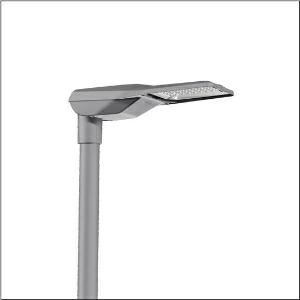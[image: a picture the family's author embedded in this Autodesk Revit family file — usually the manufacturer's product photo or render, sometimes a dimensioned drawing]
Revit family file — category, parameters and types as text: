
# Revit family: streetlight_sl_21_iq_mini___st1_0a_5xe2d41g08hb_63a2
name_source: partatom
category: Lighting Fixtures
units: mm (PartAtom-declared; Revit-internal decimal feet)

## family parameters
Cut with Voids When Loaded = No
Host = Face
Light Source = No
Part Type = Normal
Room Calculation Point = No
Round Connector Dimension = Use Diameter
Shared = No

## types (1)
- --- (1 x LED, 9860 lm, 70.9 W, 4000K)
    Apparent Load = 71 VA
    CIE Flux Codes = 37 72 97 100 100
    Color Rendering = 70
    Color Temperature = 4000K
    Default Elevation = 1800 mm
    Description = Streetlight SL 21 iQ mini, mast luminaire, primary light control with lens, of PMMA, primary optical cover: cover, of toughened safety glass, transparent, light distribution: ST1.0a, light emission: direct distribution, primary light characteristic: asymmetric, installation type: post-top, side-entry, LED, High Power LED, rated luminous flux: 9.860lm, luminous efficacy: 139lm/W, light colour: 740, colour temperature: 4000K, control: Street-Remote, Auto-Match, Temp-Guard, Lumen-Switch, Night-Set, Smart-Wire, Light-Fading, Desk-Remote (wireless, voltage-free reading and setting of iQ features in the workshop via application-optimized NFC function/RFID function), optimised constant luminous flux control (CLO 2.0), presetting dimming linear, mains connection: 220..240V, AC, 50/60Hz, start of lifetime: 71W, end of service life: 75W, reduction: 31W, luminaire housing, of diecast aluminium, powder-coated, Siteco® metallic grey (DB 702S), corrosivity category C5 mid according to DIN EN ISO 12944, please order mast flange separately, inclination adjustable: 0°, 5°, 10°, 15°, sealing non-destructively replaceable, multi-level sealing system, length: 628mm, width: 235mm, height: 110mm, mast flange for spigot size: 42mm (side-entry): 5XC10008XM4, 60/48mm (side-entry/post-top): 5XC10108XM2, 76/60mm (side-entry/post-top): 5XC10108XM1, protection rating (complete): IP66, insulation class (complete): insulation class II (safety insulation), certification: CE, ENEC, ENEC+, VDE, impact resistance: IK09, permissible operating ambient temperature for outdoor applications: -40..+50°C, standard-compliant lighting for roads and squares, packaging unit: 1 piece

Light Distribution: ST1.0a
    Height = 110 mm
    Lamp = 1 x LED
    Lamp Light Flux = 9860 lm
    Lamp Power = 70.9 W
    Lamp count = 1
    Length = 625 mm
    Luminous efficacy = 139 lm/W
    Manufacturer = Siteco
    ModVariant = No
    Model = 5XE2D41G08HB
    Number of Poles = 1
    OnlyDefault = Yes
    Power Factor = 1
    Product Name = Streetlight SL 21 iQ mini | ST1.0a
    Product group = mast luminaire | pylon top
    ProductGroupID = 6100
    Protection Class = Protection class II
    Protection Degree = IP 66
    RLX_Detail_Level = 1
    RLX_Emergency_Light_Flux = 0 lm
    RLX_Emergency_Type = 0
    RLX_Emergency_Type_DB = No
    RlxData = <blob elided: 92197 chars, md5=4411a9a7>
    Socket = socket
    Standby Power = 0 W
    System Light Flux = 9860 lm
    System Power = 71 W
    Type Comments = factory setting: luminous flux: 100 % | dim-lin: 254 | 711 mA
    Type Image = l_1003519.jpg
    URL = http://relux.com
    VarID = @adj_108233
    Voltage = 0 V
    Weight = 0.00 kg
    Width = 234 mm

## geometry (parser evidence)
native form markers: Blend x4, Sweep x10
no freeform markers — native parametric forms only
